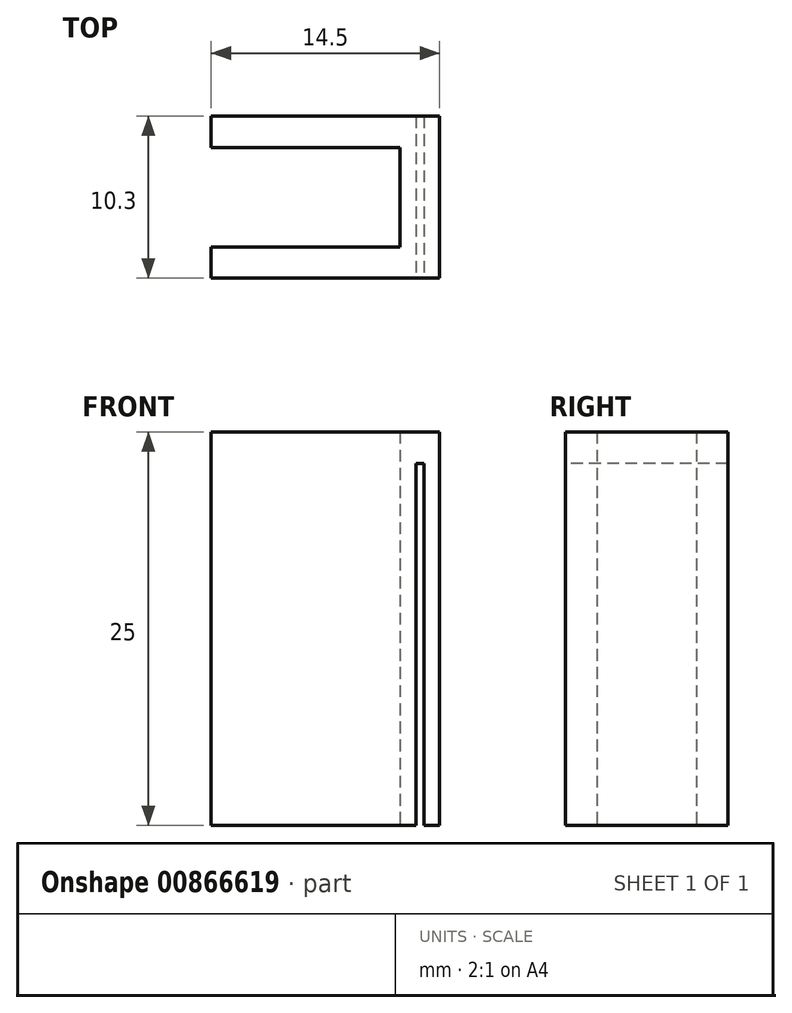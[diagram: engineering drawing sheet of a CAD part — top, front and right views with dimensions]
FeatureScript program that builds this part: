
annotation { "Feature Type Name" : "Feature", "Feature Type Description" : "" }
export const myFeature = defineFeature(function(context is Context, id is Id, definition is map)
    precondition{}
    {
        {
            var Q0;
            Q0=qCreatedBy(makeId("Top.planeOp"),FACE);
            var sketch = newSketch(context, id + "F0", { "sketchPlane" : qUnion([Q0])});
            skLineSegment(sketch, "E0.bottom", {"start": v(-10, 5.15) * mm, "end": v(2, 5.15) * mm});
            skLineSegment(sketch, "E0.top", {"start": v(-10, 3.15) * mm, "end": v(2, 3.15) * mm});
            skLineSegment(sketch, "E0.left", {"start": v(-10, 5.15) * mm, "end": v(-10, 3.15) * mm});
            skLineSegment(sketch, "E0.right", {"start": v(2, 5.15) * mm, "end": v(2, 3.15) * mm});
            skLineSegment(sketch, "E1.bottom", {"start": v(-10, -3.15) * mm, "end": v(2, -3.15) * mm});
            skLineSegment(sketch, "E1.top", {"start": v(-10, -5.15) * mm, "end": v(2, -5.15) * mm});
            skLineSegment(sketch, "E1.left", {"start": v(-10, -3.15) * mm, "end": v(-10, -5.15) * mm});
            skLineSegment(sketch, "E1.right", {"start": v(2, -3.15) * mm, "end": v(2, -5.15) * mm});
            skLineSegment(sketch, "E2.bottom", {"start": v(0, 3.15) * mm, "end": v(2, 3.15) * mm});
            skLineSegment(sketch, "E2.top", {"start": v(0, -3.15) * mm, "end": v(2, -3.15) * mm});
            skLineSegment(sketch, "E2.left", {"start": v(0, 3.15) * mm, "end": v(0, -3.15) * mm});
            skLineSegment(sketch, "E2.right", {"start": v(2, 3.15) * mm, "end": v(2, -3.15) * mm});
            skLineSegment(sketch, "E3", {"start": v(-10, 5.15) * mm, "end": v(15, 5.15) * mm});
            skLineSegment(sketch, "E4", {"start": v(15, 5.15) * mm, "end": v(15, 6.15) * mm});
            skLineSegment(sketch, "E5", {"start": v(15, 6.15) * mm, "end": v(-10, 6.15) * mm});
            skLineSegment(sketch, "E6", {"start": v(-10, 6.15) * mm, "end": v(-10, 5.15) * mm});
            skLineSegment(sketch, "E7.bottom", {"start": v(-10, 6.15) * mm, "end": v(-8, 6.15) * mm});
            skLineSegment(sketch, "E7.top", {"start": v(-10, 6.65) * mm, "end": v(-8, 6.65) * mm});
            skLineSegment(sketch, "E7.left", {"start": v(-10, 6.15) * mm, "end": v(-10, 6.65) * mm});
            skLineSegment(sketch, "E7.right", {"start": v(-8, 6.15) * mm, "end": v(-8, 6.65) * mm});
            skLineSegment(sketch, "E8.bottom", {"start": v(-10, 6.65) * mm, "end": v(15, 6.65) * mm});
            skLineSegment(sketch, "E8.top", {"start": v(-10, 7.65) * mm, "end": v(15, 7.65) * mm});
            skLineSegment(sketch, "E8.left", {"start": v(-10, 6.65) * mm, "end": v(-10, 7.65) * mm});
            skLineSegment(sketch, "E8.right", {"start": v(15, 6.65) * mm, "end": v(15, 7.65) * mm});
            skLineSegment(sketch, "E9.bottom", {"start": v(15, 6.65) * mm, "end": v(14.5, 6.65) * mm});
            skLineSegment(sketch, "E9.top", {"start": v(15, 6.3) * mm, "end": v(14.5, 6.3) * mm});
            skLineSegment(sketch, "E9.left", {"start": v(15, 6.65) * mm, "end": v(15, 6.3) * mm});
            skLineSegment(sketch, "E9.right", {"start": v(14.5, 6.65) * mm, "end": v(14.5, 6.3) * mm});
            skSolve(sketch);
        }
        {
            var Q0;
            Q0=makeQuery(id+"F0.imprint","IMPRINT",FACE,{"disambiguationData":[TD([[makeQuery(id+"F0.imprint","IMPRINT",EDGE,{"derivedFrom":sQuery(id+"F0.wireOp",EDGE,"E0.top")}),1.0]])]});
            var Q1;
            Q1=makeQuery(id+"F0.imprint","IMPRINT",FACE,{"disambiguationData":[TD([[makeQuery(id+"F0.imprint","IMPRINT",EDGE,{"derivedFrom":sQuery(id+"F0.wireOp",EDGE,"E2.bottom")}),-1.0]])]});
            var Q2;
            Q2=makeQuery(id+"F0.imprint","IMPRINT",FACE,{"disambiguationData":[TD([[makeQuery(id+"F0.imprint","IMPRINT",EDGE,{"derivedFrom":sQuery(id+"F0.wireOp",EDGE,"E1.bottom")}),-1.0]])]});
            extrude(context, id + "F1", {"entities" : qUnion([Q0, Q1, Q2]), "depth" : 25 * mm, "offsetDistance" : 25 * mm});
        }
        {
            var Q0;
            Q0=makeQuery(id+"F1.opExtrude","SWEPT_FACE",FACE,{"disambiguationData":[OSD([sQuery(id+"F0.wireOp",EDGE,"E1.top")])]});
            var sketch = newSketch(context, id + "F2", { "sketchPlane" : qUnion([Q0])});
            skLineSegment(sketch, "E10", {"start": v(2, 25) * mm, "end": v(2, 0) * mm});
            skLineSegment(sketch, "E11", {"start": v(2, 0) * mm, "end": v(3, 0) * mm});
            skLineSegment(sketch, "E12", {"start": v(3, 0) * mm, "end": v(3, 25) * mm});
            skLineSegment(sketch, "E13", {"start": v(3, 25) * mm, "end": v(2, 25) * mm});
            skLineSegment(sketch, "E14.top", {"start": v(3.5, 25) * mm, "end": v(3.5, 23) * mm});
            skLineSegment(sketch, "E14.left", {"start": v(3, 25) * mm, "end": v(3.5, 25) * mm});
            skLineSegment(sketch, "E14.right", {"start": v(3, 23) * mm, "end": v(3.5, 23) * mm});
            skLineSegment(sketch, "E15.bottom", {"start": v(3.5, 25) * mm, "end": v(3.5, 0) * mm});
            skLineSegment(sketch, "E15.top", {"start": v(4.5, 25) * mm, "end": v(4.5, 0) * mm});
            skLineSegment(sketch, "E15.left", {"start": v(3.5, 25) * mm, "end": v(4.5, 25) * mm});
            skLineSegment(sketch, "E15.right", {"start": v(3.5, 0) * mm, "end": v(4.5, 0) * mm});
            skLineSegment(sketch, "E16.bottom", {"start": v(3.5, 0) * mm, "end": v(3.5, 0.5) * mm});
            skLineSegment(sketch, "E16.top", {"start": v(3.15, 0) * mm, "end": v(3.15, 0.5) * mm});
            skLineSegment(sketch, "E16.left", {"start": v(3.5, 0) * mm, "end": v(3.15, 0) * mm});
            skLineSegment(sketch, "E16.right", {"start": v(3.5, 0.5) * mm, "end": v(3.15, 0.5) * mm});
            skSolve(sketch);
        }
        {
            var Q0;
            Q0=makeQuery(id+"F2.imprint","IMPRINT",FACE,{"disambiguationData":[TD([[makeQuery(id+"F2.imprint","IMPRINT",EDGE,{"derivedFrom":sQuery(id+"F2.wireOp",EDGE,"E15.top")}),-1.0]])]});
            var Q1;
            Q1=makeQuery(id+"F2.imprint","IMPRINT",FACE,{"disambiguationData":[TD([[makeQuery(id+"F2.imprint","IMPRINT",EDGE,{"derivedFrom":sQuery(id+"F2.wireOp",EDGE,"E10")}),1.0]])]});
            var Q2;
            {var subQ0=sQuery(id+"F2.wireOp",EDGE,"E14.left");Q2=makeQuery(id+"F2.imprint","IMPRINT",FACE,{"disambiguationData":[TD([[makeQuery(id+"F2.imprint","IMPRINT",EDGE,{"derivedFrom":subQ0}),-1.0]])]});}
            var Q3;
            Q3=makeQuery(id+"F2.imprint","IMPRINT",FACE,{"disambiguationData":[TD([[makeQuery(id+"F2.imprint","IMPRINT",EDGE,{"derivedFrom":sQuery(id+"F2.wireOp",EDGE,"E16.bottom")}),1.0]])]});
            extrude(context, id + "F3", {"entities" : qUnion([Q0, Q1, Q2, Q3]), "operationType" : NewBodyOperationType.ADD, "oppositeDirection" : true, "depth" : 10.3 * mm, "offsetDistance" : 25 * mm});
        }
    });
